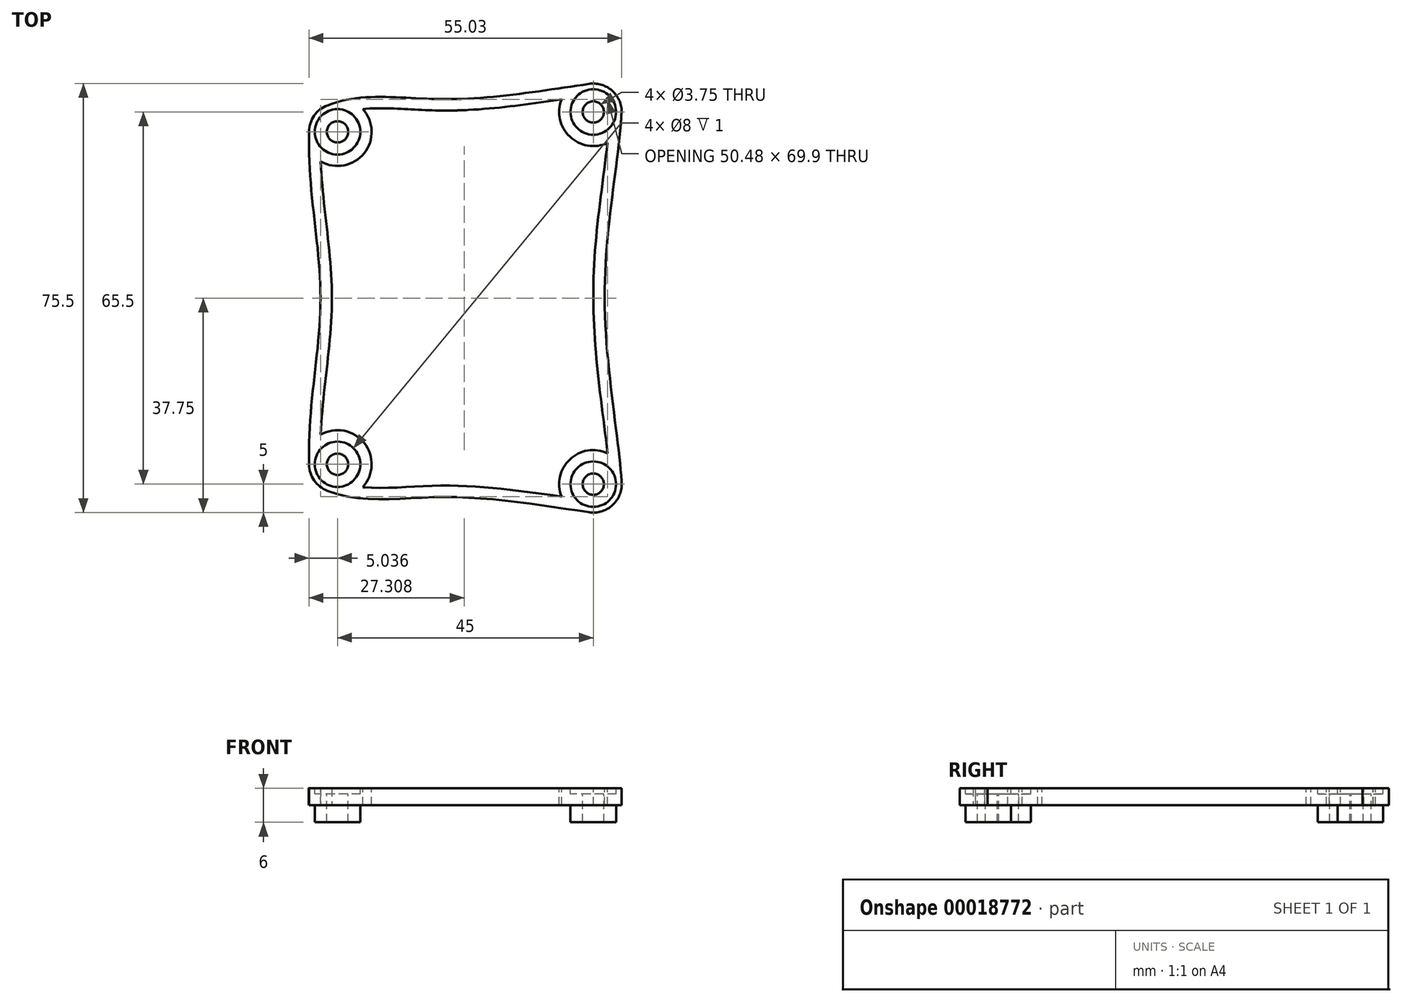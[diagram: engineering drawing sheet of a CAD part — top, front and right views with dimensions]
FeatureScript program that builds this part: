
annotation { "Feature Type Name" : "Feature", "Feature Type Description" : "" }
export const myFeature = defineFeature(function(context is Context, id is Id, definition is map)
    precondition{}
    {
        {
            var Q0;
            Q0=qCreatedBy(makeId("Top.planeOp"),FACE);
            var sketch = newSketch(context, id + "F0", { "sketchPlane" : qUnion([Q0])});
            skLineSegment(sketch, "E0", {"start": v(-18.5, 0) * mm, "end": v(-18.5, 29.25) * mm});
            skLineSegment(sketch, "E1", {"start": v(26.5, 0) * mm, "end": v(26.5, 32.75) * mm});
            skLineSegment(sketch, "E2.MirrorCS", {"start": v(26.5, 0) * mm, "end": v(26.5, -32.75) * mm});
            skLineSegment(sketch, "E3.MirrorCS", {"start": v(-18.5, 0) * mm, "end": v(-18.5, -29.25) * mm});
            skLineSegment(sketch, "E4", {"start": v(-18.5, 29.25) * mm, "end": v(26.5, -32.75) * mm});
            skLineSegment(sketch, "E5", {"start": v(26.5, 32.75) * mm, "end": v(-18.5, -29.25) * mm});
            skLineSegment(sketch, "E6", {"start": v(-18.5, 29.25) * mm, "end": v(-21.44, 33.3) * mm});
            skLineSegment(sketch, "E7", {"start": v(-18.5, -29.25) * mm, "end": v(-21.44, -33.3) * mm});
            skLineSegment(sketch, "E8", {"start": v(26.5, -32.75) * mm, "end": v(29.43, -36.8) * mm});
            skLineSegment(sketch, "E9", {"start": v(26.5, 32.75) * mm, "end": v(29.43, 36.8) * mm});
            skCircle(sketch, "E10", {"center": v(26.5, 32.75) * mm, "radius": 5 * mm});
            skCircle(sketch, "E11", {"center": v(-18.5, 29.25) * mm, "radius": 5 * mm});
            skCircle(sketch, "E12", {"center": v(-18.5, -29.25) * mm, "radius": 5 * mm});
            skCircle(sketch, "E13", {"center": v(26.5, -32.75) * mm, "radius": 5 * mm});
            skLineSegment(sketch, "E14", {"start": v(0, 0) * mm, "end": v(0, 35) * mm});
            skFitSpline(sketch, "E15", {"points": [v(-20.3, 33.91) * mm, v(0, 35) * mm, v(25.76, 37.7) * mm], "startDerivative": vector(40.76, 15.73) * mm, "endDerivative": vector(46.47, 6.88) * mm});
            skLineSegment(sketch, "E16", {"start": v(-18.5, 0) * mm, "end": v(-21.5, 0) * mm});
            skFitSpline(sketch, "E17", {"points": [v(-23.5, 29.27) * mm, v(-21.5, 0) * mm, v(-23.5, -29.3) * mm], "startDerivative": vector(-2.23, -60.22) * mm, "endDerivative": vector(2.24, -60.85) * mm});
            skLineSegment(sketch, "E18", {"start": v(26.5, 0) * mm, "end": v(28.5, 0) * mm});
            skFitSpline(sketch, "E19", {"points": [v(31.48, 33.12) * mm, v(28.5, 0) * mm, v(31.5, -32.86) * mm], "startDerivative": vector(-2.43, -54.76) * mm, "endDerivative": vector(1.51, -42.73) * mm});
            skFitSpline(sketch, "E20.MirrorCS", {"points": [v(-20.3, -33.91) * mm, v(0, -35) * mm, v(25.76, -37.7) * mm], "startDerivative": vector(40.76, -15.73) * mm, "endDerivative": vector(46.47, -6.88) * mm});
            skCircle(sketch, "E21", {"center": v(-18.5, 29.25) * mm, "radius": 1.88 * mm});
            skCircle(sketch, "E22", {"center": v(26.5, 32.75) * mm, "radius": 1.88 * mm});
            skCircle(sketch, "E23.MirrorC", {"center": v(26.5, -32.75) * mm, "radius": 1.88 * mm});
            skCircle(sketch, "E24.MirrorC", {"center": v(-18.5, -29.25) * mm, "radius": 1.88 * mm});
            skCircle(sketch, "E25", {"center": v(-18.5, 29.25) * mm, "radius": 4 * mm});
            skCircle(sketch, "E26", {"center": v(26.5, 32.75) * mm, "radius": 4 * mm});
            skCircle(sketch, "E27.MirrorC", {"center": v(26.5, -32.75) * mm, "radius": 4 * mm});
            skCircle(sketch, "E28.MirrorC", {"center": v(-18.5, -29.25) * mm, "radius": 4 * mm});
            skSolve(sketch);
        }
        {
            var Q0;
            {var subQ0=sQuery(id+"F0.wireOp",EDGE,"E28.MirrorC");var subQ3=sQuery(id+"F0.wireOp",EDGE,"E5");var subQ4=makeQuery(id+"F0.imprint","INTERSECT",VERTEX,{"derivedFrom":[subQ3,subQ0]});Q0=makeQuery(id+"F0.imprint","IMPRINT",FACE,{"disambiguationData":[TD([[makeQuery(id+"F0.imprint","IMPRINT",EDGE,{"disambiguationData":[TD([[subQ4,-1.0]])],"derivedFrom":subQ3}),1.0]])]});}
            var Q1;
            {var subQ0=sQuery(id+"F0.wireOp",EDGE,"E26");var subQ3=sQuery(id+"F0.wireOp",EDGE,"E1");var subQ4=makeQuery(id+"F0.imprint","INTERSECT",VERTEX,{"derivedFrom":[subQ3,subQ0]});Q1=makeQuery(id+"F0.imprint","IMPRINT",FACE,{"disambiguationData":[TD([[makeQuery(id+"F0.imprint","IMPRINT",EDGE,{"disambiguationData":[TD([[subQ4,-1.0]])],"derivedFrom":subQ3}),1.0]])]});}
            var Q2;
            {var subQ3=sQuery(id+"F0.wireOp",EDGE,"E2.MirrorCS");var subQ5=sQuery(id+"F0.wireOp",EDGE,"E13");var subQ7=makeQuery(id+"F0.imprint","INTERSECT",VERTEX,{"derivedFrom":[subQ3,subQ5]});Q2=makeQuery(id+"F0.imprint","IMPRINT",FACE,{"disambiguationData":[TD([[makeQuery(id+"F0.imprint","IMPRINT",EDGE,{"disambiguationData":[TD([[subQ7,-1.0]])],"derivedFrom":subQ3}),-1.0]])]});}
            var Q3;
            {var subQ3=sQuery(id+"F0.wireOp",EDGE,"E5");var subQ5=sQuery(id+"F0.wireOp",EDGE,"E12");var subQ6=makeQuery(id+"F0.imprint","INTERSECT",VERTEX,{"derivedFrom":[subQ3,subQ5]});Q3=makeQuery(id+"F0.imprint","IMPRINT",FACE,{"disambiguationData":[TD([[makeQuery(id+"F0.imprint","IMPRINT",EDGE,{"disambiguationData":[TD([[subQ6,-1.0]])],"derivedFrom":subQ3}),1.0]])]});}
            var Q4;
            {var subQ3=sQuery(id+"F0.wireOp",EDGE,"E1");var subQ6=sQuery(id+"F0.wireOp",EDGE,"E10");var subQ9=makeQuery(id+"F0.imprint","INTERSECT",VERTEX,{"derivedFrom":[subQ3,subQ6]});Q4=makeQuery(id+"F0.imprint","IMPRINT",FACE,{"disambiguationData":[TD([[makeQuery(id+"F0.imprint","IMPRINT",EDGE,{"disambiguationData":[TD([[subQ9,-1.0]])],"derivedFrom":subQ3}),-1.0]])]});}
            var Q5;
            {var subQ1=sQuery(id+"F0.wireOp",EDGE,"E5");var subQ6=sQuery(id+"F0.wireOp",EDGE,"E26");var subQ8=makeQuery(id+"F0.imprint","INTERSECT",VERTEX,{"derivedFrom":[subQ1,subQ6]});Q5=makeQuery(id+"F0.imprint","IMPRINT",FACE,{"disambiguationData":[TD([[makeQuery(id+"F0.imprint","IMPRINT",EDGE,{"disambiguationData":[TD([[subQ8,-1.0]])],"derivedFrom":subQ1}),-1.0]])]});}
            var Q6;
            {var subQ0=sQuery(id+"F0.wireOp",EDGE,"E28.MirrorC");var subQ3=sQuery(id+"F0.wireOp",EDGE,"E3.MirrorCS");var subQ4=makeQuery(id+"F0.imprint","INTERSECT",VERTEX,{"derivedFrom":[subQ3,subQ0]});Q6=makeQuery(id+"F0.imprint","IMPRINT",FACE,{"disambiguationData":[TD([[makeQuery(id+"F0.imprint","IMPRINT",EDGE,{"disambiguationData":[TD([[subQ4,-1.0]])],"derivedFrom":subQ3}),-1.0]])]});}
            var Q7;
            {var subQ3=sQuery(id+"F0.wireOp",EDGE,"E14");var subQ5=sQuery(id+"F0.wireOp",EDGE,"E4");var subQ6=makeQuery(id+"F0.imprint","INTERSECT",VERTEX,{"derivedFrom":[subQ5,subQ3]});Q7=makeQuery(id+"F0.imprint","IMPRINT",FACE,{"disambiguationData":[TD([[makeQuery(id+"F0.imprint","IMPRINT",EDGE,{"disambiguationData":[TD([[subQ6,1.0]])],"derivedFrom":subQ5}),1.0]])]});}
            var Q8;
            {var subQ0=sQuery(id+"F0.wireOp",EDGE,"E14");var subQ1=sQuery(id+"F0.wireOp",EDGE,"E4");var subQ2=makeQuery(id+"F0.imprint","INTERSECT",VERTEX,{"derivedFrom":[subQ1,subQ0]});Q8=makeQuery(id+"F0.imprint","IMPRINT",FACE,{"disambiguationData":[TD([[makeQuery(id+"F0.imprint","IMPRINT",EDGE,{"disambiguationData":[TD([[subQ2,-1.0]])],"derivedFrom":subQ1}),1.0]])]});}
            var Q9;
            {var subQ3=sQuery(id+"F0.wireOp",EDGE,"E2.MirrorCS");var subQ5=sQuery(id+"F0.wireOp",EDGE,"E13");var subQ7=makeQuery(id+"F0.imprint","INTERSECT",VERTEX,{"derivedFrom":[subQ3,subQ5]});Q9=makeQuery(id+"F0.imprint","IMPRINT",FACE,{"disambiguationData":[TD([[makeQuery(id+"F0.imprint","IMPRINT",EDGE,{"disambiguationData":[TD([[subQ7,-1.0]])],"derivedFrom":subQ3}),1.0]])]});}
            var Q10;
            {var subQ3=sQuery(id+"F0.wireOp",EDGE,"E8");var subQ5=sQuery(id+"F0.wireOp",EDGE,"E13");var subQ7=makeQuery(id+"F0.imprint","INTERSECT",VERTEX,{"derivedFrom":[subQ3,subQ5]});Q10=makeQuery(id+"F0.imprint","IMPRINT",FACE,{"disambiguationData":[TD([[makeQuery(id+"F0.imprint","IMPRINT",EDGE,{"disambiguationData":[TD([[subQ7,1.0]])],"derivedFrom":subQ3}),1.0]])]});}
            var Q11;
            {var subQ0=sQuery(id+"F0.wireOp",EDGE,"E27.MirrorC");var subQ3=sQuery(id+"F0.wireOp",EDGE,"E2.MirrorCS");var subQ4=makeQuery(id+"F0.imprint","INTERSECT",VERTEX,{"derivedFrom":[subQ3,subQ0]});Q11=makeQuery(id+"F0.imprint","IMPRINT",FACE,{"disambiguationData":[TD([[makeQuery(id+"F0.imprint","IMPRINT",EDGE,{"disambiguationData":[TD([[subQ4,-1.0]])],"derivedFrom":subQ3}),1.0]])]});}
            var Q12;
            {var subQ3=sQuery(id+"F0.wireOp",EDGE,"E1");var subQ5=sQuery(id+"F0.wireOp",EDGE,"E10");var subQ7=makeQuery(id+"F0.imprint","INTERSECT",VERTEX,{"derivedFrom":[subQ3,subQ5]});Q12=makeQuery(id+"F0.imprint","IMPRINT",FACE,{"disambiguationData":[TD([[makeQuery(id+"F0.imprint","IMPRINT",EDGE,{"disambiguationData":[TD([[subQ7,-1.0]])],"derivedFrom":subQ3}),1.0]])]});}
            var Q13;
            {var subQ3=sQuery(id+"F0.wireOp",EDGE,"E16");Q13=makeQuery(id+"F0.imprint","IMPRINT",FACE,{"disambiguationData":[TD([[makeQuery(id+"F0.imprint","IMPRINT",EDGE,{"derivedFrom":subQ3}),1.0]])]});}
            var Q14;
            {var subQ0=sQuery(id+"F0.wireOp",EDGE,"E27.MirrorC");var subQ3=sQuery(id+"F0.wireOp",EDGE,"E4");var subQ4=makeQuery(id+"F0.imprint","INTERSECT",VERTEX,{"derivedFrom":[subQ3,subQ0]});Q14=makeQuery(id+"F0.imprint","IMPRINT",FACE,{"disambiguationData":[TD([[makeQuery(id+"F0.imprint","IMPRINT",EDGE,{"disambiguationData":[TD([[subQ4,-1.0]])],"derivedFrom":subQ3}),-1.0]])]});}
            var Q15;
            {var subQ0=sQuery(id+"F0.wireOp",EDGE,"E25");var subQ3=sQuery(id+"F0.wireOp",EDGE,"E0");var subQ4=makeQuery(id+"F0.imprint","INTERSECT",VERTEX,{"derivedFrom":[subQ3,subQ0]});Q15=makeQuery(id+"F0.imprint","IMPRINT",FACE,{"disambiguationData":[TD([[makeQuery(id+"F0.imprint","IMPRINT",EDGE,{"disambiguationData":[TD([[subQ4,-1.0]])],"derivedFrom":subQ3}),1.0]])]});}
            var Q16;
            {var subQ3=sQuery(id+"F0.wireOp",EDGE,"E4");var subQ5=sQuery(id+"F0.wireOp",EDGE,"E21");var subQ7=makeQuery(id+"F0.imprint","INTERSECT",VERTEX,{"derivedFrom":[subQ3,subQ5]});Q16=makeQuery(id+"F0.imprint","IMPRINT",FACE,{"disambiguationData":[TD([[makeQuery(id+"F0.imprint","IMPRINT",EDGE,{"disambiguationData":[TD([[subQ7,-1.0]])],"derivedFrom":subQ3}),1.0]])]});}
            var Q17;
            {var subQ3=sQuery(id+"F0.wireOp",EDGE,"E5");var subQ5=sQuery(id+"F0.wireOp",EDGE,"E22");var subQ7=makeQuery(id+"F0.imprint","INTERSECT",VERTEX,{"derivedFrom":[subQ3,subQ5]});Q17=makeQuery(id+"F0.imprint","IMPRINT",FACE,{"disambiguationData":[TD([[makeQuery(id+"F0.imprint","IMPRINT",EDGE,{"disambiguationData":[TD([[subQ7,-1.0]])],"derivedFrom":subQ3}),-1.0]])]});}
            var Q18;
            {var subQ0=sQuery(id+"F0.wireOp",EDGE,"E27.MirrorC");var subQ3=sQuery(id+"F0.wireOp",EDGE,"E2.MirrorCS");var subQ4=makeQuery(id+"F0.imprint","INTERSECT",VERTEX,{"derivedFrom":[subQ3,subQ0]});Q18=makeQuery(id+"F0.imprint","IMPRINT",FACE,{"disambiguationData":[TD([[makeQuery(id+"F0.imprint","IMPRINT",EDGE,{"disambiguationData":[TD([[subQ4,-1.0]])],"derivedFrom":subQ3}),-1.0]])]});}
            var Q19;
            {var subQ0=sQuery(id+"F0.wireOp",EDGE,"E28.MirrorC");var subQ3=sQuery(id+"F0.wireOp",EDGE,"E3.MirrorCS");var subQ4=makeQuery(id+"F0.imprint","INTERSECT",VERTEX,{"derivedFrom":[subQ3,subQ0]});Q19=makeQuery(id+"F0.imprint","IMPRINT",FACE,{"disambiguationData":[TD([[makeQuery(id+"F0.imprint","IMPRINT",EDGE,{"disambiguationData":[TD([[subQ4,-1.0]])],"derivedFrom":subQ3}),1.0]])]});}
            var Q20;
            {var subQ1=sQuery(id+"F0.wireOp",EDGE,"E19");var subQ3=sQuery(id+"F0.wireOp",EDGE,"E8");var subQ5=makeQuery(id+"F0.imprint","INTERSECT",VERTEX,{"derivedFrom":[subQ3,subQ1]});Q20=makeQuery(id+"F0.imprint","IMPRINT",FACE,{"disambiguationData":[TD([[makeQuery(id+"F0.imprint","IMPRINT",EDGE,{"disambiguationData":[TD([[subQ5,-1.0]])],"derivedFrom":subQ3}),1.0]])]});}
            var Q21;
            {var subQ0=sQuery(id+"F0.wireOp",EDGE,"E25");var subQ3=sQuery(id+"F0.wireOp",EDGE,"E0");var subQ4=makeQuery(id+"F0.imprint","INTERSECT",VERTEX,{"derivedFrom":[subQ3,subQ0]});Q21=makeQuery(id+"F0.imprint","IMPRINT",FACE,{"disambiguationData":[TD([[makeQuery(id+"F0.imprint","IMPRINT",EDGE,{"disambiguationData":[TD([[subQ4,-1.0]])],"derivedFrom":subQ3}),-1.0]])]});}
            var Q22;
            {var subQ3=sQuery(id+"F0.wireOp",EDGE,"E13");var subQ5=sQuery(id+"F0.wireOp",EDGE,"E4");var subQ8=makeQuery(id+"F0.imprint","INTERSECT",VERTEX,{"derivedFrom":[subQ5,subQ3]});Q22=makeQuery(id+"F0.imprint","IMPRINT",FACE,{"disambiguationData":[TD([[makeQuery(id+"F0.imprint","IMPRINT",EDGE,{"disambiguationData":[TD([[subQ8,-1.0]])],"derivedFrom":subQ5}),-1.0]])]});}
            var Q23;
            {var subQ3=sQuery(id+"F0.wireOp",EDGE,"E3.MirrorCS");var subQ5=sQuery(id+"F0.wireOp",EDGE,"E12");var subQ8=makeQuery(id+"F0.imprint","INTERSECT",VERTEX,{"derivedFrom":[subQ3,subQ5]});Q23=makeQuery(id+"F0.imprint","IMPRINT",FACE,{"disambiguationData":[TD([[makeQuery(id+"F0.imprint","IMPRINT",EDGE,{"disambiguationData":[TD([[subQ8,-1.0]])],"derivedFrom":subQ3}),-1.0]])]});}
            var Q24;
            {var subQ1=sQuery(id+"F0.wireOp",EDGE,"E4");var subQ11=makeQuery(id+"F0.imprint","INTERSECT",VERTEX,{"derivedFrom":[subQ1,sQuery(id+"F0.wireOp",EDGE,"E14")]});Q24=makeQuery(id+"F0.imprint","IMPRINT",FACE,{"disambiguationData":[TD([[makeQuery(id+"F0.imprint","IMPRINT",EDGE,{"disambiguationData":[TD([[subQ11,1.0]])],"derivedFrom":subQ1}),-1.0]])]});}
            var Q25;
            {var subQ3=sQuery(id+"F0.wireOp",EDGE,"E0");var subQ5=sQuery(id+"F0.wireOp",EDGE,"E11");var subQ8=makeQuery(id+"F0.imprint","INTERSECT",VERTEX,{"derivedFrom":[subQ3,subQ5]});Q25=makeQuery(id+"F0.imprint","IMPRINT",FACE,{"disambiguationData":[TD([[makeQuery(id+"F0.imprint","IMPRINT",EDGE,{"disambiguationData":[TD([[subQ8,-1.0]])],"derivedFrom":subQ3}),1.0]])]});}
            var Q26;
            {var subQ0=sQuery(id+"F0.wireOp",EDGE,"E20.MirrorCS");Q26=makeQuery(id+"F0.imprint","IMPRINT",FACE,{"disambiguationData":[TD([[makeQuery(id+"F0.imprint","IMPRINT",EDGE,{"derivedFrom":subQ0}),1.0]])]});}
            var Q27;
            {var subQ3=sQuery(id+"F0.wireOp",EDGE,"E3.MirrorCS");var subQ5=sQuery(id+"F0.wireOp",EDGE,"E12");var subQ7=makeQuery(id+"F0.imprint","INTERSECT",VERTEX,{"derivedFrom":[subQ3,subQ5]});Q27=makeQuery(id+"F0.imprint","IMPRINT",FACE,{"disambiguationData":[TD([[makeQuery(id+"F0.imprint","IMPRINT",EDGE,{"disambiguationData":[TD([[subQ7,-1.0]])],"derivedFrom":subQ3}),1.0]])]});}
            var Q28;
            {var subQ1=sQuery(id+"F0.wireOp",EDGE,"E4");var subQ6=sQuery(id+"F0.wireOp",EDGE,"E5");var subQ10=makeQuery(id+"F0.imprint","INTERSECT",VERTEX,{"derivedFrom":[subQ1,subQ6]});Q28=makeQuery(id+"F0.imprint","IMPRINT",FACE,{"disambiguationData":[TD([[makeQuery(id+"F0.imprint","IMPRINT",EDGE,{"disambiguationData":[TD([[subQ10,-1.0]])],"derivedFrom":subQ1}),1.0]])]});}
            var Q29;
            {var subQ3=sQuery(id+"F0.wireOp",EDGE,"E18");Q29=makeQuery(id+"F0.imprint","IMPRINT",FACE,{"disambiguationData":[TD([[makeQuery(id+"F0.imprint","IMPRINT",EDGE,{"derivedFrom":subQ3}),-1.0]])]});}
            var Q30;
            {var subQ3=sQuery(id+"F0.wireOp",EDGE,"E0");var subQ5=sQuery(id+"F0.wireOp",EDGE,"E11");var subQ7=makeQuery(id+"F0.imprint","INTERSECT",VERTEX,{"derivedFrom":[subQ3,subQ5]});Q30=makeQuery(id+"F0.imprint","IMPRINT",FACE,{"disambiguationData":[TD([[makeQuery(id+"F0.imprint","IMPRINT",EDGE,{"disambiguationData":[TD([[subQ7,-1.0]])],"derivedFrom":subQ3}),-1.0]])]});}
            var Q31;
            {var subQ3=sQuery(id+"F0.wireOp",EDGE,"E16");Q31=makeQuery(id+"F0.imprint","IMPRINT",FACE,{"disambiguationData":[TD([[makeQuery(id+"F0.imprint","IMPRINT",EDGE,{"derivedFrom":subQ3}),-1.0]])]});}
            var Q32;
            {var subQ0=sQuery(id+"F0.wireOp",EDGE,"E18");Q32=makeQuery(id+"F0.imprint","IMPRINT",FACE,{"disambiguationData":[TD([[makeQuery(id+"F0.imprint","IMPRINT",EDGE,{"derivedFrom":subQ0}),1.0]])]});}
            var Q33;
            {var subQ0=sQuery(id+"F0.wireOp",EDGE,"E26");var subQ3=sQuery(id+"F0.wireOp",EDGE,"E1");var subQ4=makeQuery(id+"F0.imprint","INTERSECT",VERTEX,{"derivedFrom":[subQ3,subQ0]});Q33=makeQuery(id+"F0.imprint","IMPRINT",FACE,{"disambiguationData":[TD([[makeQuery(id+"F0.imprint","IMPRINT",EDGE,{"disambiguationData":[TD([[subQ4,-1.0]])],"derivedFrom":subQ3}),-1.0]])]});}
            var Q34;
            {var subQ0=sQuery(id+"F0.wireOp",EDGE,"E25");var subQ3=sQuery(id+"F0.wireOp",EDGE,"E4");var subQ4=makeQuery(id+"F0.imprint","INTERSECT",VERTEX,{"derivedFrom":[subQ3,subQ0]});Q34=makeQuery(id+"F0.imprint","IMPRINT",FACE,{"disambiguationData":[TD([[makeQuery(id+"F0.imprint","IMPRINT",EDGE,{"disambiguationData":[TD([[subQ4,-1.0]])],"derivedFrom":subQ3}),1.0]])]});}
            var Q35;
            {var subQ3=sQuery(id+"F0.wireOp",EDGE,"E8");var subQ5=sQuery(id+"F0.wireOp",EDGE,"E13");var subQ7=makeQuery(id+"F0.imprint","INTERSECT",VERTEX,{"derivedFrom":[subQ3,subQ5]});Q35=makeQuery(id+"F0.imprint","IMPRINT",FACE,{"disambiguationData":[TD([[makeQuery(id+"F0.imprint","IMPRINT",EDGE,{"disambiguationData":[TD([[subQ7,1.0]])],"derivedFrom":subQ3}),-1.0]])]});}
            var Q36;
            {var subQ1=sQuery(id+"F0.wireOp",EDGE,"E19");var subQ3=sQuery(id+"F0.wireOp",EDGE,"E8");var subQ5=makeQuery(id+"F0.imprint","INTERSECT",VERTEX,{"derivedFrom":[subQ3,subQ1]});Q36=makeQuery(id+"F0.imprint","IMPRINT",FACE,{"disambiguationData":[TD([[makeQuery(id+"F0.imprint","IMPRINT",EDGE,{"disambiguationData":[TD([[subQ5,-1.0]])],"derivedFrom":subQ3}),-1.0]])]});}
            extrude(context, id + "F1", {"entities" : qUnion([Q0, Q1, Q2, Q3, Q4, Q5, Q6, Q7, Q8, Q9, Q10, Q11, Q12, Q13, Q14, Q15, Q16, Q17, Q18, Q19, Q20, Q21, Q22, Q23, Q24, Q25, Q26, Q27, Q28, Q29, Q30, Q31, Q32, Q33, Q34, Q35, Q36]), "oppositeDirection" : true, "depth" : 3 * mm});
        }
        {
            var Q0;
            {var subQ0=sQuery(id+"F0.wireOp",EDGE,"E28.MirrorC");var subQ3=sQuery(id+"F0.wireOp",EDGE,"E3.MirrorCS");var subQ4=makeQuery(id+"F0.imprint","INTERSECT",VERTEX,{"derivedFrom":[subQ3,subQ0]});Q0=makeQuery(id+"F0.imprint","IMPRINT",FACE,{"disambiguationData":[TD([[makeQuery(id+"F0.imprint","IMPRINT",EDGE,{"disambiguationData":[TD([[subQ4,-1.0]])],"derivedFrom":subQ3}),-1.0]])]});}
            var Q1;
            {var subQ0=sQuery(id+"F0.wireOp",EDGE,"E28.MirrorC");var subQ3=sQuery(id+"F0.wireOp",EDGE,"E5");var subQ4=makeQuery(id+"F0.imprint","INTERSECT",VERTEX,{"derivedFrom":[subQ3,subQ0]});Q1=makeQuery(id+"F0.imprint","IMPRINT",FACE,{"disambiguationData":[TD([[makeQuery(id+"F0.imprint","IMPRINT",EDGE,{"disambiguationData":[TD([[subQ4,-1.0]])],"derivedFrom":subQ3}),1.0]])]});}
            var Q2;
            {var subQ0=sQuery(id+"F0.wireOp",EDGE,"E28.MirrorC");var subQ3=sQuery(id+"F0.wireOp",EDGE,"E3.MirrorCS");var subQ4=makeQuery(id+"F0.imprint","INTERSECT",VERTEX,{"derivedFrom":[subQ3,subQ0]});Q2=makeQuery(id+"F0.imprint","IMPRINT",FACE,{"disambiguationData":[TD([[makeQuery(id+"F0.imprint","IMPRINT",EDGE,{"disambiguationData":[TD([[subQ4,-1.0]])],"derivedFrom":subQ3}),1.0]])]});}
            var Q3;
            {var subQ0=sQuery(id+"F0.wireOp",EDGE,"E27.MirrorC");var subQ3=sQuery(id+"F0.wireOp",EDGE,"E4");var subQ4=makeQuery(id+"F0.imprint","INTERSECT",VERTEX,{"derivedFrom":[subQ3,subQ0]});Q3=makeQuery(id+"F0.imprint","IMPRINT",FACE,{"disambiguationData":[TD([[makeQuery(id+"F0.imprint","IMPRINT",EDGE,{"disambiguationData":[TD([[subQ4,-1.0]])],"derivedFrom":subQ3}),-1.0]])]});}
            var Q4;
            {var subQ0=sQuery(id+"F0.wireOp",EDGE,"E27.MirrorC");var subQ3=sQuery(id+"F0.wireOp",EDGE,"E2.MirrorCS");var subQ4=makeQuery(id+"F0.imprint","INTERSECT",VERTEX,{"derivedFrom":[subQ3,subQ0]});Q4=makeQuery(id+"F0.imprint","IMPRINT",FACE,{"disambiguationData":[TD([[makeQuery(id+"F0.imprint","IMPRINT",EDGE,{"disambiguationData":[TD([[subQ4,-1.0]])],"derivedFrom":subQ3}),1.0]])]});}
            var Q5;
            {var subQ1=sQuery(id+"F0.wireOp",EDGE,"E19");var subQ3=sQuery(id+"F0.wireOp",EDGE,"E8");var subQ5=makeQuery(id+"F0.imprint","INTERSECT",VERTEX,{"derivedFrom":[subQ3,subQ1]});Q5=makeQuery(id+"F0.imprint","IMPRINT",FACE,{"disambiguationData":[TD([[makeQuery(id+"F0.imprint","IMPRINT",EDGE,{"disambiguationData":[TD([[subQ5,-1.0]])],"derivedFrom":subQ3}),1.0]])]});}
            var Q6;
            {var subQ0=sQuery(id+"F0.wireOp",EDGE,"E27.MirrorC");var subQ3=sQuery(id+"F0.wireOp",EDGE,"E2.MirrorCS");var subQ4=makeQuery(id+"F0.imprint","INTERSECT",VERTEX,{"derivedFrom":[subQ3,subQ0]});Q6=makeQuery(id+"F0.imprint","IMPRINT",FACE,{"disambiguationData":[TD([[makeQuery(id+"F0.imprint","IMPRINT",EDGE,{"disambiguationData":[TD([[subQ4,-1.0]])],"derivedFrom":subQ3}),-1.0]])]});}
            var Q7;
            {var subQ3=sQuery(id+"F0.wireOp",EDGE,"E5");var subQ5=sQuery(id+"F0.wireOp",EDGE,"E22");var subQ7=makeQuery(id+"F0.imprint","INTERSECT",VERTEX,{"derivedFrom":[subQ3,subQ5]});Q7=makeQuery(id+"F0.imprint","IMPRINT",FACE,{"disambiguationData":[TD([[makeQuery(id+"F0.imprint","IMPRINT",EDGE,{"disambiguationData":[TD([[subQ7,-1.0]])],"derivedFrom":subQ3}),-1.0]])]});}
            var Q8;
            {var subQ0=sQuery(id+"F0.wireOp",EDGE,"E26");var subQ3=sQuery(id+"F0.wireOp",EDGE,"E1");var subQ4=makeQuery(id+"F0.imprint","INTERSECT",VERTEX,{"derivedFrom":[subQ3,subQ0]});Q8=makeQuery(id+"F0.imprint","IMPRINT",FACE,{"disambiguationData":[TD([[makeQuery(id+"F0.imprint","IMPRINT",EDGE,{"disambiguationData":[TD([[subQ4,-1.0]])],"derivedFrom":subQ3}),-1.0]])]});}
            var Q9;
            {var subQ3=sQuery(id+"F0.wireOp",EDGE,"E4");var subQ5=sQuery(id+"F0.wireOp",EDGE,"E21");var subQ7=makeQuery(id+"F0.imprint","INTERSECT",VERTEX,{"derivedFrom":[subQ3,subQ5]});Q9=makeQuery(id+"F0.imprint","IMPRINT",FACE,{"disambiguationData":[TD([[makeQuery(id+"F0.imprint","IMPRINT",EDGE,{"disambiguationData":[TD([[subQ7,-1.0]])],"derivedFrom":subQ3}),1.0]])]});}
            var Q10;
            {var subQ0=sQuery(id+"F0.wireOp",EDGE,"E25");var subQ3=sQuery(id+"F0.wireOp",EDGE,"E0");var subQ4=makeQuery(id+"F0.imprint","INTERSECT",VERTEX,{"derivedFrom":[subQ3,subQ0]});Q10=makeQuery(id+"F0.imprint","IMPRINT",FACE,{"disambiguationData":[TD([[makeQuery(id+"F0.imprint","IMPRINT",EDGE,{"disambiguationData":[TD([[subQ4,-1.0]])],"derivedFrom":subQ3}),1.0]])]});}
            var Q11;
            {var subQ0=sQuery(id+"F0.wireOp",EDGE,"E25");var subQ3=sQuery(id+"F0.wireOp",EDGE,"E0");var subQ4=makeQuery(id+"F0.imprint","INTERSECT",VERTEX,{"derivedFrom":[subQ3,subQ0]});Q11=makeQuery(id+"F0.imprint","IMPRINT",FACE,{"disambiguationData":[TD([[makeQuery(id+"F0.imprint","IMPRINT",EDGE,{"disambiguationData":[TD([[subQ4,-1.0]])],"derivedFrom":subQ3}),-1.0]])]});}
            var Q12;
            {var subQ0=sQuery(id+"F0.wireOp",EDGE,"E26");var subQ3=sQuery(id+"F0.wireOp",EDGE,"E1");var subQ4=makeQuery(id+"F0.imprint","INTERSECT",VERTEX,{"derivedFrom":[subQ3,subQ0]});Q12=makeQuery(id+"F0.imprint","IMPRINT",FACE,{"disambiguationData":[TD([[makeQuery(id+"F0.imprint","IMPRINT",EDGE,{"disambiguationData":[TD([[subQ4,-1.0]])],"derivedFrom":subQ3}),1.0]])]});}
            extrude(context, id + "F2", {"entities" : qUnion([Q0, Q1, Q2, Q3, Q4, Q5, Q6, Q7, Q8, Q9, Q10, Q11, Q12]), "operationType" : NewBodyOperationType.ADD, "oppositeDirection" : true, "depth" : 6 * mm});
        }
        {
            var Q0;
            {var subQ0=sQuery(id+"F0.wireOp",EDGE,"E28.MirrorC");var subQ3=sQuery(id+"F0.wireOp",EDGE,"E3.MirrorCS");var subQ4=makeQuery(id+"F0.imprint","INTERSECT",VERTEX,{"derivedFrom":[subQ3,subQ0]});Q0=makeQuery(id+"F0.imprint","IMPRINT",FACE,{"disambiguationData":[TD([[makeQuery(id+"F0.imprint","IMPRINT",EDGE,{"disambiguationData":[TD([[subQ4,-1.0]])],"derivedFrom":subQ3}),-1.0]])]});}
            var Q1;
            {var subQ0=sQuery(id+"F0.wireOp",EDGE,"E28.MirrorC");var subQ3=sQuery(id+"F0.wireOp",EDGE,"E3.MirrorCS");var subQ4=makeQuery(id+"F0.imprint","INTERSECT",VERTEX,{"derivedFrom":[subQ3,subQ0]});Q1=makeQuery(id+"F0.imprint","IMPRINT",FACE,{"disambiguationData":[TD([[makeQuery(id+"F0.imprint","IMPRINT",EDGE,{"disambiguationData":[TD([[subQ4,-1.0]])],"derivedFrom":subQ3}),1.0]])]});}
            var Q2;
            {var subQ0=sQuery(id+"F0.wireOp",EDGE,"E28.MirrorC");var subQ3=sQuery(id+"F0.wireOp",EDGE,"E5");var subQ4=makeQuery(id+"F0.imprint","INTERSECT",VERTEX,{"derivedFrom":[subQ3,subQ0]});Q2=makeQuery(id+"F0.imprint","IMPRINT",FACE,{"disambiguationData":[TD([[makeQuery(id+"F0.imprint","IMPRINT",EDGE,{"disambiguationData":[TD([[subQ4,-1.0]])],"derivedFrom":subQ3}),1.0]])]});}
            var Q3;
            {var subQ0=sQuery(id+"F0.wireOp",EDGE,"E27.MirrorC");var subQ3=sQuery(id+"F0.wireOp",EDGE,"E4");var subQ4=makeQuery(id+"F0.imprint","INTERSECT",VERTEX,{"derivedFrom":[subQ3,subQ0]});Q3=makeQuery(id+"F0.imprint","IMPRINT",FACE,{"disambiguationData":[TD([[makeQuery(id+"F0.imprint","IMPRINT",EDGE,{"disambiguationData":[TD([[subQ4,-1.0]])],"derivedFrom":subQ3}),-1.0]])]});}
            var Q4;
            {var subQ0=sQuery(id+"F0.wireOp",EDGE,"E27.MirrorC");var subQ3=sQuery(id+"F0.wireOp",EDGE,"E2.MirrorCS");var subQ4=makeQuery(id+"F0.imprint","INTERSECT",VERTEX,{"derivedFrom":[subQ3,subQ0]});Q4=makeQuery(id+"F0.imprint","IMPRINT",FACE,{"disambiguationData":[TD([[makeQuery(id+"F0.imprint","IMPRINT",EDGE,{"disambiguationData":[TD([[subQ4,-1.0]])],"derivedFrom":subQ3}),-1.0]])]});}
            var Q5;
            {var subQ0=sQuery(id+"F0.wireOp",EDGE,"E27.MirrorC");var subQ3=sQuery(id+"F0.wireOp",EDGE,"E2.MirrorCS");var subQ4=makeQuery(id+"F0.imprint","INTERSECT",VERTEX,{"derivedFrom":[subQ3,subQ0]});Q5=makeQuery(id+"F0.imprint","IMPRINT",FACE,{"disambiguationData":[TD([[makeQuery(id+"F0.imprint","IMPRINT",EDGE,{"disambiguationData":[TD([[subQ4,-1.0]])],"derivedFrom":subQ3}),1.0]])]});}
            var Q6;
            {var subQ3=sQuery(id+"F0.wireOp",EDGE,"E5");var subQ5=sQuery(id+"F0.wireOp",EDGE,"E22");var subQ7=makeQuery(id+"F0.imprint","INTERSECT",VERTEX,{"derivedFrom":[subQ3,subQ5]});Q6=makeQuery(id+"F0.imprint","IMPRINT",FACE,{"disambiguationData":[TD([[makeQuery(id+"F0.imprint","IMPRINT",EDGE,{"disambiguationData":[TD([[subQ7,-1.0]])],"derivedFrom":subQ3}),-1.0]])]});}
            var Q7;
            {var subQ0=sQuery(id+"F0.wireOp",EDGE,"E26");var subQ3=sQuery(id+"F0.wireOp",EDGE,"E1");var subQ4=makeQuery(id+"F0.imprint","INTERSECT",VERTEX,{"derivedFrom":[subQ3,subQ0]});Q7=makeQuery(id+"F0.imprint","IMPRINT",FACE,{"disambiguationData":[TD([[makeQuery(id+"F0.imprint","IMPRINT",EDGE,{"disambiguationData":[TD([[subQ4,-1.0]])],"derivedFrom":subQ3}),1.0]])]});}
            var Q8;
            {var subQ0=sQuery(id+"F0.wireOp",EDGE,"E26");var subQ3=sQuery(id+"F0.wireOp",EDGE,"E1");var subQ4=makeQuery(id+"F0.imprint","INTERSECT",VERTEX,{"derivedFrom":[subQ3,subQ0]});Q8=makeQuery(id+"F0.imprint","IMPRINT",FACE,{"disambiguationData":[TD([[makeQuery(id+"F0.imprint","IMPRINT",EDGE,{"disambiguationData":[TD([[subQ4,-1.0]])],"derivedFrom":subQ3}),-1.0]])]});}
            var Q9;
            {var subQ3=sQuery(id+"F0.wireOp",EDGE,"E0");var subQ5=sQuery(id+"F0.wireOp",EDGE,"E25");var subQ7=makeQuery(id+"F0.imprint","INTERSECT",VERTEX,{"derivedFrom":[subQ3,subQ5]});Q9=makeQuery(id+"F0.imprint","IMPRINT",FACE,{"disambiguationData":[TD([[makeQuery(id+"F0.imprint","IMPRINT",EDGE,{"disambiguationData":[TD([[subQ7,-1.0]])],"derivedFrom":subQ3}),1.0]])]});}
            var Q10;
            {var subQ3=sQuery(id+"F0.wireOp",EDGE,"E4");var subQ5=sQuery(id+"F0.wireOp",EDGE,"E21");var subQ7=makeQuery(id+"F0.imprint","INTERSECT",VERTEX,{"derivedFrom":[subQ3,subQ5]});Q10=makeQuery(id+"F0.imprint","IMPRINT",FACE,{"disambiguationData":[TD([[makeQuery(id+"F0.imprint","IMPRINT",EDGE,{"disambiguationData":[TD([[subQ7,-1.0]])],"derivedFrom":subQ3}),1.0]])]});}
            var Q11;
            {var subQ0=sQuery(id+"F0.wireOp",EDGE,"E25");var subQ3=sQuery(id+"F0.wireOp",EDGE,"E0");var subQ4=makeQuery(id+"F0.imprint","INTERSECT",VERTEX,{"derivedFrom":[subQ3,subQ0]});Q11=makeQuery(id+"F0.imprint","IMPRINT",FACE,{"disambiguationData":[TD([[makeQuery(id+"F0.imprint","IMPRINT",EDGE,{"disambiguationData":[TD([[subQ4,-1.0]])],"derivedFrom":subQ3}),-1.0]])]});}
            extrude(context, id + "F3", {"entities" : qUnion([Q0, Q1, Q2, Q3, Q4, Q5, Q6, Q7, Q8, Q9, Q10, Q11]), "operationType" : NewBodyOperationType.REMOVE, "oppositeDirection" : true, "depth" : 1 * mm});
        }
        {
            var Q0;
            Q0=makeQuery(id+"F1.opExtrude","CAP_FACE",FACE,{"disambiguationData":[OSD([sQuery(id+"F0.wireOp",EDGE,"E10"),sQuery(id+"F0.wireOp",EDGE,"E11"),sQuery(id+"F0.wireOp",EDGE,"E12"),sQuery(id+"F0.wireOp",EDGE,"E13"),sQuery(id+"F0.wireOp",EDGE,"E15"),sQuery(id+"F0.wireOp",EDGE,"E17"),sQuery(id+"F0.wireOp",EDGE,"E19"),sQuery(id+"F0.wireOp",EDGE,"E20.MirrorCS"),sQuery(id+"F0.wireOp",EDGE,"E21"),sQuery(id+"F0.wireOp",EDGE,"E22"),sQuery(id+"F0.wireOp",EDGE,"E23.MirrorC"),sQuery(id+"F0.wireOp",EDGE,"E24.MirrorC")])],"isStart":false});
            var Q1;
            Q1=makeQuery(id+"F1.opExtrude","CAP_FACE",FACE,{"disambiguationData":[OSD([sQuery(id+"F0.wireOp",EDGE,"E10"),sQuery(id+"F0.wireOp",EDGE,"E11"),sQuery(id+"F0.wireOp",EDGE,"E12"),sQuery(id+"F0.wireOp",EDGE,"E13"),sQuery(id+"F0.wireOp",EDGE,"E15"),sQuery(id+"F0.wireOp",EDGE,"E17"),sQuery(id+"F0.wireOp",EDGE,"E19"),sQuery(id+"F0.wireOp",EDGE,"E20.MirrorCS"),sQuery(id+"F0.wireOp",EDGE,"E21"),sQuery(id+"F0.wireOp",EDGE,"E22"),sQuery(id+"F0.wireOp",EDGE,"E23.MirrorC"),sQuery(id+"F0.wireOp",EDGE,"E24.MirrorC")])],"isStart":true});
            shell(context, id + "F4", {"entities" : qUnion([Q0, Q1]), "thickness" : 2 * mm});
        }
    });
